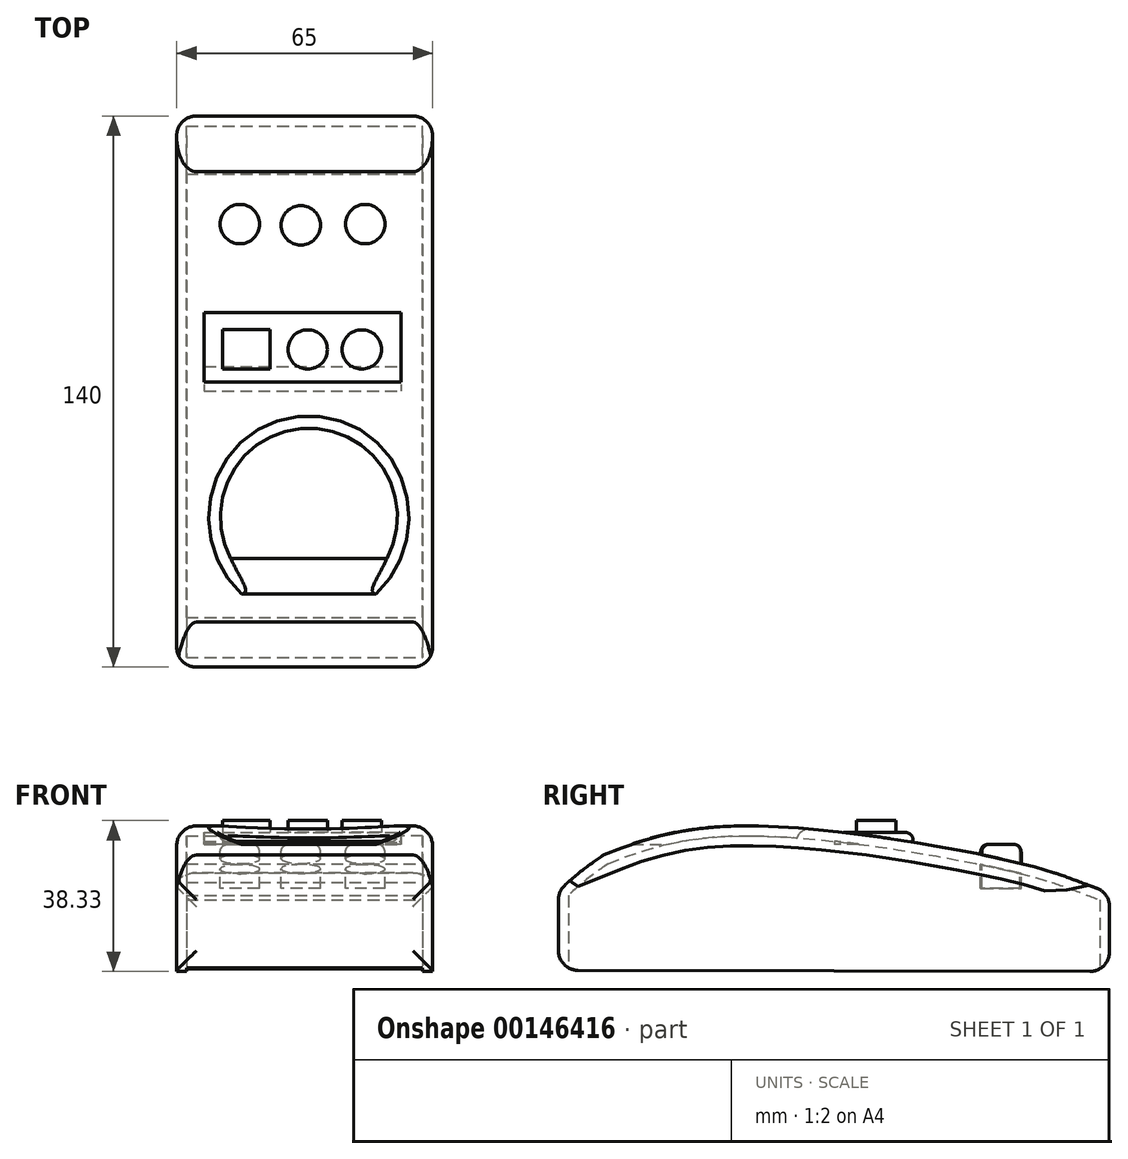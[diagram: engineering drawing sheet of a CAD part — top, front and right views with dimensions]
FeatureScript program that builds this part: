
annotation { "Feature Type Name" : "Feature", "Feature Type Description" : "" }
export const myFeature = defineFeature(function(context is Context, id is Id, definition is map)
    precondition{}
    {
        {
            var Q0;
            Q0=qCreatedBy(makeId("Right.planeOp"),FACE);
            var sketch = newSketch(context, id + "F0", { "sketchPlane" : qUnion([Q0])});
            skFitSpline(sketch, "E0", {"points": [v(-56.25, -2.75) * mm, v(-24.23, 4.56) * mm, v(51.63, -5.37) * mm, v(58.2, -7.23) * mm], "startDerivative": vector(59.7, 24.02) * mm, "endDerivative": vector(3.58, 0.78) * mm});
            skFitSpline(sketch, "E1", {"points": [v(-56.25, -2.75) * mm, v(-67.69, -12.05) * mm, v(-67.7, -12.34) * mm], "startDerivative": vector(-20.98, -14.03) * mm, "endDerivative": vector(3.3, -1.5) * mm});
            skFitSpline(sketch, "E2", {"points": [v(58.2, -7.23) * mm, v(72.31, -12.34) * mm], "startDerivative": vector(20.34, -7.09) * mm, "endDerivative": vector(20.34, -7.09) * mm});
            skLineSegment(sketch, "E3", {"start": v(72.31, -12.34) * mm, "end": v(72.31, -32.34) * mm});
            skLineSegment(sketch, "E4", {"start": v(-67.69, -12.05) * mm, "end": v(-67.69, -32.05) * mm});
            skLineSegment(sketch, "E5", {"start": v(72.31, -32.34) * mm, "end": v(-67.69, -32.05) * mm});
            skSolve(sketch);
        }
        {
            var Q0;
            {var subQ0=sQuery(id+"F0.wireOp",EDGE,"E0");Q0=makeQuery(id+"F0.imprint","IMPRINT",FACE,{"disambiguationData":[TD([[makeQuery(id+"F0.imprint","IMPRINT",EDGE,{"derivedFrom":subQ0}),-1.0]])]});}
            extrude(context, id + "F1", {"entities" : qUnion([Q0]), "oppositeDirection" : true, "depth" : 65 * mm});
        }
        {
            var Q0;
            Q0=makeQuery(id+"F1.opExtrude","SWEPT_FACE",FACE,{"disambiguationData":[OSD([sQuery(id+"F0.wireOp",EDGE,"E5")])]});
            shell(context, id + "F2", {"entities" : qUnion([Q0]), "thickness" : 2.5 * mm});
        }
        {
            var Q0;
            Q0=qCreatedBy(makeId("Top.planeOp"),FACE);
            var sketch = newSketch(context, id + "F3", { "sketchPlane" : qUnion([Q0])});
            skCircle(sketch, "E6", {"center": v(-31.42, -29.49) * mm, "radius": 22.5 * mm});
            skSolve(sketch);
        }
        {
            var Q0;
            Q0 = qSketchRegion(id + "F3", true);
            extrude(context, id + "F4", {"entities" : qUnion([Q0]), "operationType" : NewBodyOperationType.REMOVE, "depth" : 5 * mm});
        }
        {
            var Q0;
            Q0=makeQuery(id+"F1.opExtrude","CAP_EDGE",EDGE,{"disambiguationData":[OSD([sQuery(id+"F0.wireOp",EDGE,"E0")])],"isStart":true});
            var Q1;
            Q1=makeQuery(id+"F1.opExtrude","CAP_EDGE",EDGE,{"disambiguationData":[OSD([sQuery(id+"F0.wireOp",EDGE,"E0")])],"isStart":false});
            var Q2;
            Q2=makeQuery(id+"F1.opExtrude","SWEPT_FACE",FACE,{"disambiguationData":[OSD([sQuery(id+"F0.wireOp",EDGE,"E4")])]});
            var Q3;
            Q3=makeQuery(id+"F1.opExtrude","SWEPT_EDGE",EDGE,{"disambiguationData":[OSD([sQuery(id+"F0.wireOp",EDGE,"E2"),sQuery(id+"F0.wireOp",EDGE,"E3")])]});
            var Q4;
            Q4=makeQuery(id+"F1.opExtrude","SWEPT_FACE",FACE,{"disambiguationData":[OSD([sQuery(id+"F0.wireOp",EDGE,"E3")])]});
            fillet(context, id + "F5", {"entities" : qUnion([Q0, Q1, Q2, Q3, Q4]), "radius" : 5 * mm, "tangentPropagation" : true, "allowEdgeOverflow" : false});
        }
        {
            var Q0;
            Q0=qCreatedBy(makeId("Top.planeOp"),FACE);
            var sketch = newSketch(context, id + "F6", { "sketchPlane" : qUnion([Q0])});
            skCircle(sketch, "E7", {"center": v(-48.94, 44.85) * mm, "radius": 5 * mm});
            skCircle(sketch, "E8", {"center": v(-33.46, 44.56) * mm, "radius": 5 * mm});
            skCircle(sketch, "E9", {"center": v(-17.1, 44.85) * mm, "radius": 5 * mm});
            skSolve(sketch);
        }
        {
            var Q0;
            Q0 = qSketchRegion(id + "F6", true);
            extrude(context, id + "F7", {"entities" : qUnion([Q0]), "operationType" : NewBodyOperationType.ADD, "oppositeDirection" : true, "depth" : 11.25 * mm});
        }
        {
            var Q0;
            Q0=qCreatedBy(makeId("Top.planeOp"),FACE);
            var sketch = newSketch(context, id + "F8", { "sketchPlane" : qUnion([Q0])});
            skLineSegment(sketch, "E10.bottom", {"start": v(-8, 22.42) * mm, "end": v(-58, 22.42) * mm});
            skLineSegment(sketch, "E10.top", {"start": v(-8, 2.42) * mm, "end": v(-58, 2.42) * mm});
            skLineSegment(sketch, "E10.left", {"start": v(-8, 22.42) * mm, "end": v(-8, 2.42) * mm});
            skLineSegment(sketch, "E10.right", {"start": v(-58, 22.42) * mm, "end": v(-58, 2.42) * mm});
            skPoint(sketch, "E10.middle", {"position": v(-33, 12.42) * mm});
            skSolve(sketch);
        }
        {
            var Q0;
            Q0=makeQuery(id+"F8.imprint","IMPRINT",FACE,{"disambiguationData":[TD([[makeQuery(id+"F8.imprint","IMPRINT",EDGE,{"derivedFrom":sQuery(id+"F8.wireOp",EDGE,"E10.bottom")}),1.0]])]});
            extrude(context, id + "F9", {"entities" : qUnion([Q0]), "operationType" : NewBodyOperationType.ADD, "depth" : 3 * mm});
        }
        {
            var Q0;
            Q0=makeQuery(id+"F9.opExtrude","CAP_EDGE",EDGE,{"disambiguationData":[OSD([sQuery(id+"F8.wireOp",EDGE,"E10.bottom")])],"isStart":false});
            fillet(context, id + "F10", {"entities" : qUnion([Q0]), "radius" : 2 * mm, "tangentPropagation" : true, "allowEdgeOverflow" : false});
        }
        {
            var Q0;
            Q0=qCreatedBy(makeId("Top.planeOp"),FACE);
            var sketch = newSketch(context, id + "F11", { "sketchPlane" : qUnion([Q0])});
            skCircle(sketch, "E11", {"center": v(-17.97, 13) * mm, "radius": 5 * mm});
            skCircle(sketch, "E12", {"center": v(-31.7, 13) * mm, "radius": 5 * mm});
            skLineSegment(sketch, "E13.bottom", {"start": v(-41.33, 18.04) * mm, "end": v(-53.33, 18.04) * mm});
            skLineSegment(sketch, "E13.top", {"start": v(-41.33, 8.04) * mm, "end": v(-53.33, 8.04) * mm});
            skLineSegment(sketch, "E13.left", {"start": v(-41.33, 18.04) * mm, "end": v(-41.33, 8.04) * mm});
            skLineSegment(sketch, "E13.right", {"start": v(-53.33, 18.04) * mm, "end": v(-53.33, 8.04) * mm});
            skPoint(sketch, "E13.middle", {"position": v(-47.33, 13.04) * mm});
            skSolve(sketch);
        }
        {
            var Q0;
            Q0=sQuery(id+"F11.wireOp",EDGE,"E11");
            var Q1;
            Q1=sQuery(id+"F11.wireOp",EDGE,"E12");
            var Q2;
            Q2=sQuery(id+"F11.wireOp",EDGE,"E13.left");
            var Q3;
            Q3=sQuery(id+"F11.wireOp",EDGE,"E13.bottom");
            var Q4;
            Q4=sQuery(id+"F11.wireOp",EDGE,"E13.right");
            var Q5;
            Q5=sQuery(id+"F11.wireOp",EDGE,"E13.top");
            extrude(context, id + "F12", {"bodyType" : ToolBodyType.SURFACE, "surfaceEntities" : qUnion([Q0, Q1, Q2, Q3, Q4, Q5]), "depth" : 6 * mm});
        }
        {
            var Q0;
            Q0=makeQuery(id+"F7.opExtrude","CAP_EDGE",EDGE,{"disambiguationData":[OSD([sQuery(id+"F6.wireOp",EDGE,"E9")])],"isStart":true});
            var Q1;
            Q1=makeQuery(id+"F7.opExtrude","CAP_EDGE",EDGE,{"disambiguationData":[OSD([sQuery(id+"F6.wireOp",EDGE,"E8")])],"isStart":true});
            var Q2;
            Q2=makeQuery(id+"F7.opExtrude","CAP_EDGE",EDGE,{"disambiguationData":[OSD([sQuery(id+"F6.wireOp",EDGE,"E7")])],"isStart":true});
            fillet(context, id + "F13", {"entities" : qUnion([Q0, Q1, Q2]), "radius" : 2 * mm, "tangentPropagation" : true, "allowEdgeOverflow" : false});
        }
        {
            var Q0;
            Q0=makeQuery(id+"F4.boolean.opBoolean","INTERSECT",EDGE,{"derivedFrom":[makeQuery(id+"F1.opExtrude","SWEPT_FACE",FACE,{"disambiguationData":[OSD([sQuery(id+"F0.wireOp",EDGE,"E0")])]}),makeQuery(id+"F4.opExtrude","SWEPT_FACE",FACE,{"disambiguationData":[OSD([sQuery(id+"F3.wireOp",EDGE,"E6")])]})]});
            fillet(context, id + "F14", {"entities" : qUnion([Q0]), "radius" : 3 * mm, "tangentPropagation" : true, "allowEdgeOverflow" : false});
        }
        {
            var Q0;
            Q0 = qSketchRegion(id + "F11", true);
            extrude(context, id + "F15", {"entities" : qUnion([Q0]), "operationType" : NewBodyOperationType.ADD, "depth" : 4 * mm});
        }
        {
            var Q0;
            Q0=makeQuery(id+"F15.opExtrude","CAP_FACE",FACE,{"disambiguationData":[OSD([sQuery(id+"F11.wireOp",EDGE,"E12")])],"isStart":false});
            var Q1;
            Q1=makeQuery(id+"F15.opExtrude","CAP_FACE",FACE,{"disambiguationData":[OSD([sQuery(id+"F11.wireOp",EDGE,"E11")])],"isStart":false});
            var Q2;
            Q2=makeQuery(id+"F15.opExtrude","CAP_FACE",FACE,{"disambiguationData":[OSD([sQuery(id+"F11.wireOp",EDGE,"E13.bottom"),sQuery(id+"F11.wireOp",EDGE,"E13.top"),sQuery(id+"F11.wireOp",EDGE,"E13.left"),sQuery(id+"F11.wireOp",EDGE,"E13.right")])],"isStart":false});
            extrude(context, id + "F16", {"entities" : qUnion([Q0, Q1, Q2]), "operationType" : NewBodyOperationType.ADD, "depth" : 2 * mm});
        }
    });
